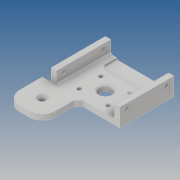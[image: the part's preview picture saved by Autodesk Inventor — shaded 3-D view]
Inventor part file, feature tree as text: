
AUTODESK INVENTOR PART (.ipt)
format: ipt  version: 2019 (Build 230136000, 136)  size: 202,752 bytes
history: native  units: mm
features: sketch x4, other x3, extrude x3, chamfer x3, hole x2, fillet x1, projected_geometry x1
ambient origin geometry x8: Origin, YZ Plane, XZ Plane, XY Plane, X Axis, Y Axis, Z Axis, Center Point
bodies: Solide1 (feature_tree)
feature tree (17):
  other  "base_cloison.ipt"
  sketch  "Esquisse1"
  hole  "Perçage1"  [1 undecoded]
  extrude  "Extrusion1"  Depth=18.0mm
  chamfer  "Chanfrein1"  Distance=40.0mm
  extrude  "Extrusion2"  Depth=47.0mm
  hole  "Perçage2"  [1 undecoded]
  chamfer  "Chanfrein3"  Distance=4.0mm
  fillet  "Congé1"  Radius=4.0mm
  extrude  "Extrusion3"  Depth=5.0mm
  chamfer  "Chanfrein4"  Distance=24.0mm
  other  "Solide1::base_cloison.ipt"
  other  "FonctionRepérage1"
  sketch  "Esquisse2"
  sketch  "Esquisse4"
  sketch  "Esquisse5"
  projected_geometry  "Boucle projetée1"
note: 2 required parameter values undecoded (feature->parameter linkage not recoverable at this tier; creation-order binding heuristic only, values carry confidence <= 0.55)
